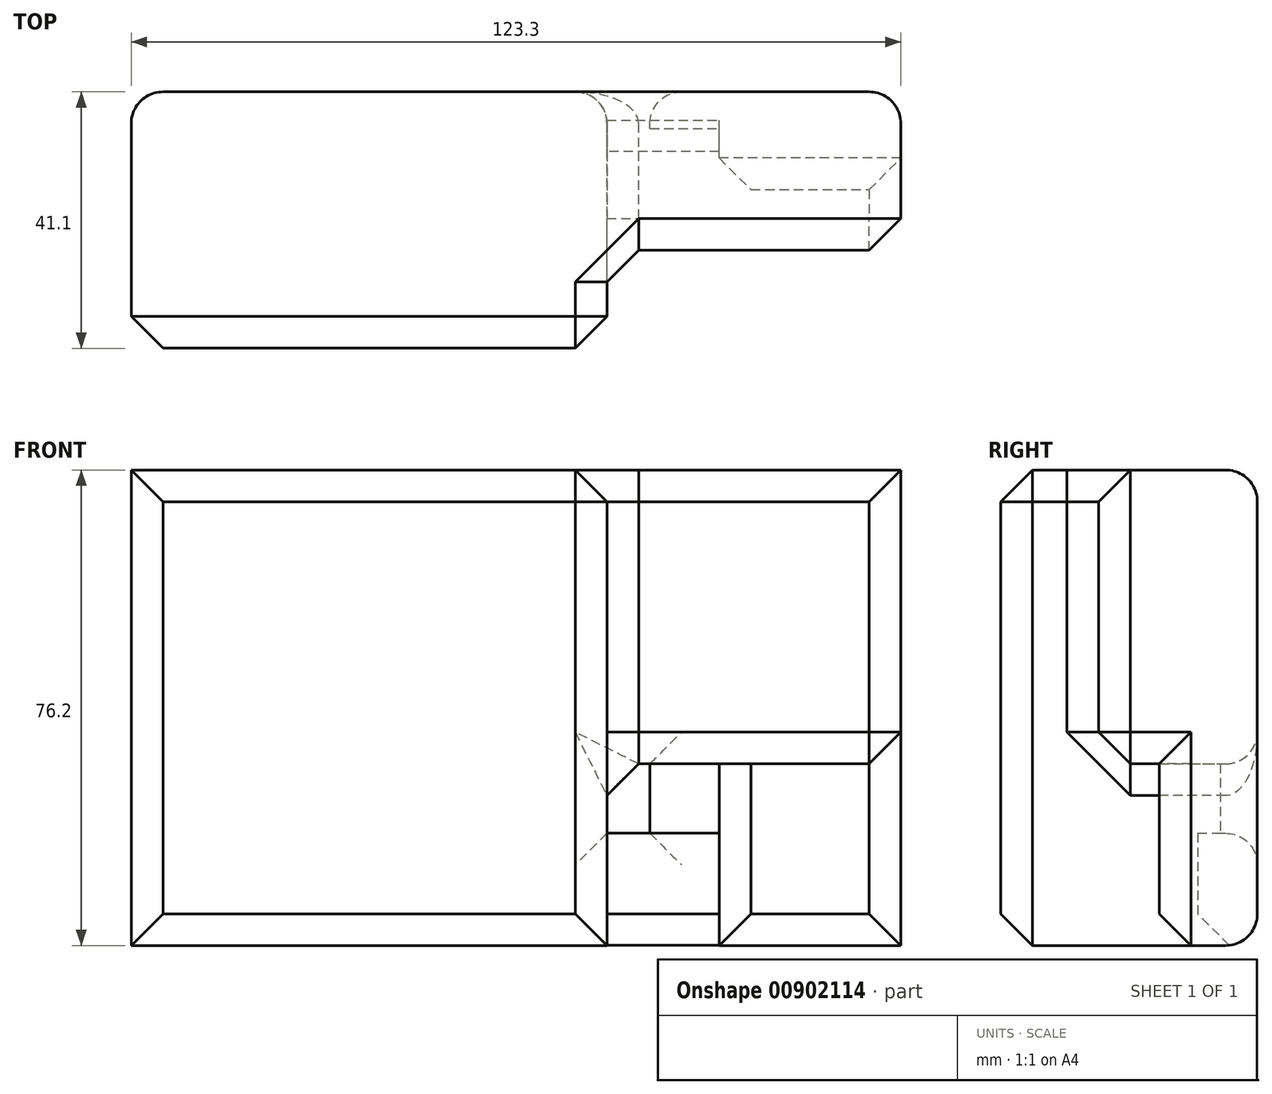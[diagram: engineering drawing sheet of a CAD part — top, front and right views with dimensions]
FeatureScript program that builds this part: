
annotation { "Feature Type Name" : "Feature", "Feature Type Description" : "" }
export const myFeature = defineFeature(function(context is Context, id is Id, definition is map)
    precondition{}
    {
        {
            var Q0;
            Q0=qCreatedBy(makeId("Front.planeOp"),FACE);
            var sketch = newSketch(context, id + "F0", { "sketchPlane" : qUnion([Q0])});
            skLineSegment(sketch, "E0.bottom", {"start": v(-61.65, -38.1) * mm, "end": v(61.65, -38.1) * mm});
            skLineSegment(sketch, "E0.top", {"start": v(-61.65, 38.1) * mm, "end": v(61.65, 38.1) * mm});
            skLineSegment(sketch, "E0.left", {"start": v(-61.65, -38.1) * mm, "end": v(-61.65, 38.1) * mm});
            skLineSegment(sketch, "E0.right", {"start": v(61.65, -38.1) * mm, "end": v(61.65, 38.1) * mm});
            skPoint(sketch, "E0.middle", {"position": v(0, 0) * mm});
            skLineSegment(sketch, "E1.bottom", {"start": v(-61.65, 38.1) * mm, "end": v(14.55, 38.1) * mm});
            skLineSegment(sketch, "E1.top", {"start": v(-61.65, -38.1) * mm, "end": v(14.55, -38.1) * mm});
            skLineSegment(sketch, "E1.left", {"start": v(-61.65, 38.1) * mm, "end": v(-61.65, -38.1) * mm});
            skLineSegment(sketch, "E1.right", {"start": v(14.55, 38.1) * mm, "end": v(14.55, -38.1) * mm});
            skLineSegment(sketch, "E2.bottom", {"start": v(14.55, 38.1) * mm, "end": v(61.65, 38.1) * mm});
            skLineSegment(sketch, "E2.top", {"start": v(14.55, -9) * mm, "end": v(61.65, -9) * mm});
            skLineSegment(sketch, "E2.left", {"start": v(14.55, 38.1) * mm, "end": v(14.55, -9) * mm});
            skLineSegment(sketch, "E2.right", {"start": v(61.65, 38.1) * mm, "end": v(61.65, -9) * mm});
            skLineSegment(sketch, "E3.bottom", {"start": v(61.65, -9) * mm, "end": v(32.54, -9) * mm});
            skLineSegment(sketch, "E3.top", {"start": v(61.65, -38.1) * mm, "end": v(32.54, -38.1) * mm});
            skLineSegment(sketch, "E3.left", {"start": v(61.65, -9) * mm, "end": v(61.65, -38.1) * mm});
            skLineSegment(sketch, "E3.right", {"start": v(32.54, -9) * mm, "end": v(32.54, -38.1) * mm});
            skLineSegment(sketch, "E4.bottom", {"start": v(32.54, -38.1) * mm, "end": v(14.55, -38.1) * mm});
            skLineSegment(sketch, "E4.top", {"start": v(32.54, -20.12) * mm, "end": v(14.55, -20.12) * mm});
            skLineSegment(sketch, "E4.left", {"start": v(32.54, -38.1) * mm, "end": v(32.54, -20.12) * mm});
            skLineSegment(sketch, "E4.right", {"start": v(14.55, -38.1) * mm, "end": v(14.55, -20.12) * mm});
            skLineSegment(sketch, "E5.bottom", {"start": v(32.54, -9) * mm, "end": v(21.44, -9) * mm});
            skLineSegment(sketch, "E5.top", {"start": v(32.54, -20.12) * mm, "end": v(21.44, -20.12) * mm});
            skLineSegment(sketch, "E5.left", {"start": v(32.54, -9) * mm, "end": v(32.54, -20.12) * mm});
            skLineSegment(sketch, "E5.right", {"start": v(21.44, -9) * mm, "end": v(21.44, -20.12) * mm});
            skSolve(sketch);
        }
        {
            var Q0;
            {var subQ4=sQuery(id+"F0.wireOp",EDGE,"E0.left");Q0=makeQuery(id+"F0.imprint","IMPRINT",FACE,{"disambiguationData":[TD([[makeQuery(id+"F0.imprint","IMPRINT",EDGE,{"derivedFrom":subQ4}),-1.0]])]});}
            extrude(context, id + "F1", {"entities" : qUnion([Q0]), "depth" : 41.1 * mm, "offsetDistance" : 25.4 * mm});
        }
        {
            var Q0;
            {var subQ1=sQuery(id+"F0.wireOp",EDGE,"E0.top");var subQ5=sQuery(id+"F0.wireOp",EDGE,"E0.right");var subQ8=makeQuery(id+"F0.imprint","INTERSECT",VERTEX,{"derivedFrom":[subQ1,subQ5]});Q0=makeQuery(id+"F0.imprint","IMPRINT",FACE,{"disambiguationData":[TD([[makeQuery(id+"F0.imprint","IMPRINT",EDGE,{"disambiguationData":[TD([[subQ8,1.0]])],"derivedFrom":subQ1}),-1.0]])]});}
            extrude(context, id + "F2", {"entities" : qUnion([Q0]), "operationType" : NewBodyOperationType.ADD, "depth" : 25.4 * mm, "offsetDistance" : 25.4 * mm});
        }
        {
            var Q0;
            {var subQ0=sQuery(id+"F0.wireOp",EDGE,"E3.right");var subQ1=sQuery(id+"F0.wireOp",EDGE,"E0.bottom");var subQ2=makeQuery(id+"F0.imprint","INTERSECT",VERTEX,{"derivedFrom":[subQ1,subQ0]});Q0=makeQuery(id+"F0.imprint","IMPRINT",FACE,{"disambiguationData":[TD([[makeQuery(id+"F0.imprint","IMPRINT",EDGE,{"disambiguationData":[TD([[subQ2,-1.0]])],"derivedFrom":subQ1}),1.0]])]});}
            extrude(context, id + "F3", {"entities" : qUnion([Q0]), "operationType" : NewBodyOperationType.ADD, "depth" : 15.7 * mm, "offsetDistance" : 25.4 * mm});
        }
        {
            var Q0;
            {var subQ1=sQuery(id+"F0.wireOp",EDGE,"E3.right");var subQ4=sQuery(id+"F0.wireOp",EDGE,"E0.bottom");var subQ5=makeQuery(id+"F0.imprint","INTERSECT",VERTEX,{"derivedFrom":[subQ4,subQ1]});Q0=makeQuery(id+"F0.imprint","IMPRINT",FACE,{"disambiguationData":[TD([[makeQuery(id+"F0.imprint","IMPRINT",EDGE,{"disambiguationData":[TD([[subQ5,1.0]])],"derivedFrom":subQ4}),1.0]])]});}
            extrude(context, id + "F4", {"entities" : qUnion([Q0]), "operationType" : NewBodyOperationType.ADD, "depth" : 9.58 * mm, "offsetDistance" : 25.4 * mm});
        }
        {
            var Q0;
            {var subQ3=sQuery(id+"F0.wireOp",EDGE,"E5.right");Q0=makeQuery(id+"F0.imprint","IMPRINT",FACE,{"disambiguationData":[TD([[makeQuery(id+"F0.imprint","IMPRINT",EDGE,{"derivedFrom":subQ3}),1.0]])]});}
            extrude(context, id + "F5", {"entities" : qUnion([Q0]), "operationType" : NewBodyOperationType.ADD, "depth" : 5.92 * mm, "offsetDistance" : 25.4 * mm});
        }
        {
            var Q0;
            Q0=makeQuery(id+"F1.opExtrude","CAP_EDGE",EDGE,{"disambiguationData":[OSD([sQuery(id+"F0.wireOp",EDGE,"E0.left")])],"isStart":true});
            var Q1;
            {var subQ0=sQuery(id+"F0.wireOp",EDGE,"E4.top");var subQ1=sQuery(id+"F0.wireOp",EDGE,"E3.right");var subQ2=sQuery(id+"F0.wireOp",EDGE,"E2.top");var subQ3=sQuery(id+"F0.wireOp",EDGE,"E1.right");var subQ4=sQuery(id+"F0.wireOp",EDGE,"E0.bottom");var subQ5=sQuery(id+"F0.wireOp",EDGE,"E0.right");var subQ6=sQuery(id+"F0.wireOp",EDGE,"E0.top");Q1=makeQuery(id+"F5.boolean.opBoolean","MERGE",FACE,{"derivedFrom":[makeQuery(id+"F4.boolean.opBoolean","MERGE",FACE,{"derivedFrom":[makeQuery(id+"F3.boolean.opBoolean","MERGE",FACE,{"derivedFrom":[makeQuery(id+"F2.boolean.opBoolean","MERGE",FACE,{"derivedFrom":[makeQuery(id+"F1.opExtrude","CAP_FACE",FACE,{"disambiguationData":[OSD([subQ4,subQ6,sQuery(id+"F0.wireOp",EDGE,"E0.left"),subQ3])],"isStart":true}),makeQuery(id+"F2.opExtrude","CAP_FACE",FACE,{"disambiguationData":[OSD([subQ6,subQ5,subQ3,subQ2])],"isStart":true})]}),makeQuery(id+"F3.opExtrude","CAP_FACE",FACE,{"disambiguationData":[OSD([subQ4,subQ5,subQ2,subQ1])],"isStart":true})]}),makeQuery(id+"F4.opExtrude","CAP_FACE",FACE,{"disambiguationData":[OSD([subQ4,subQ3,subQ1,subQ0])],"isStart":true})]}),makeQuery(id+"F5.opExtrude","CAP_FACE",FACE,{"disambiguationData":[OSD([subQ2,subQ1,subQ0,sQuery(id+"F0.wireOp",EDGE,"E5.right")])],"isStart":true})]});}
            fillet(context, id + "F6", {"entities" : qUnion([Q0, Q1]), "radius" : 5.08 * mm, "tangentPropagation" : true, "allowEdgeOverflow" : false});
        }
        {
            var Q0;
            Q0=makeQuery(id+"F1.opExtrude","CAP_EDGE",EDGE,{"disambiguationData":[OSD([sQuery(id+"F0.wireOp",EDGE,"E0.bottom")])],"isStart":false});
            var Q1;
            Q1=makeQuery(id+"F1.opExtrude","CAP_EDGE",EDGE,{"disambiguationData":[OSD([sQuery(id+"F0.wireOp",EDGE,"E1.right")])],"isStart":false});
            var Q2;
            Q2=makeQuery(id+"F1.opExtrude","CAP_EDGE",EDGE,{"disambiguationData":[OSD([sQuery(id+"F0.wireOp",EDGE,"E0.left")])],"isStart":false});
            var Q3;
            Q3=makeQuery(id+"F1.opExtrude","CAP_EDGE",EDGE,{"disambiguationData":[OSD([sQuery(id+"F0.wireOp",EDGE,"E0.top")])],"isStart":false});
            var Q4;
            Q4=makeQuery(id+"F2.opExtrude","CAP_EDGE",EDGE,{"disambiguationData":[OSD([sQuery(id+"F0.wireOp",EDGE,"E1.right")])],"isStart":false});
            var Q5;
            Q5=makeQuery(id+"F1.opExtrude","SWEPT_EDGE",EDGE,{"disambiguationData":[OSD([sQuery(id+"F0.wireOp",EDGE,"E0.top"),sQuery(id+"F0.wireOp",EDGE,"E1.right")])]});
            var Q6;
            Q6=makeQuery(id+"F2.opExtrude","CAP_FACE",FACE,{"disambiguationData":[OSD([sQuery(id+"F0.wireOp",EDGE,"E0.top"),sQuery(id+"F0.wireOp",EDGE,"E0.right"),sQuery(id+"F0.wireOp",EDGE,"E1.right"),sQuery(id+"F0.wireOp",EDGE,"E2.top")])],"isStart":false});
            var Q7;
            Q7=makeQuery(id+"F2.opExtrude","SWEPT_EDGE",EDGE,{"disambiguationData":[OSD([sQuery(id+"F0.wireOp",EDGE,"E0.right"),sQuery(id+"F0.wireOp",EDGE,"E2.top")])]});
            var Q8;
            Q8=makeQuery(id+"F3.opExtrude","CAP_EDGE",EDGE,{"disambiguationData":[OSD([sQuery(id+"F0.wireOp",EDGE,"E0.right")])],"isStart":false});
            var Q9;
            Q9=makeQuery(id+"F3.opExtrude","CAP_EDGE",EDGE,{"disambiguationData":[OSD([sQuery(id+"F0.wireOp",EDGE,"E0.bottom")])],"isStart":false});
            var Q10;
            Q10=makeQuery(id+"F3.opExtrude","CAP_EDGE",EDGE,{"disambiguationData":[OSD([sQuery(id+"F0.wireOp",EDGE,"E3.right")])],"isStart":false});
            var Q11;
            Q11=makeQuery(id+"F4.opExtrude","CAP_EDGE",EDGE,{"disambiguationData":[OSD([sQuery(id+"F0.wireOp",EDGE,"E0.bottom")])],"isStart":false});
            chamfer(context, id + "F7", {"entities" : qUnion([Q0, Q1, Q2, Q3, Q4, Q5, Q6, Q7, Q8, Q9, Q10, Q11]), "width" : 5.08 * mm, "tangentPropagation" : true});
        }
    });
